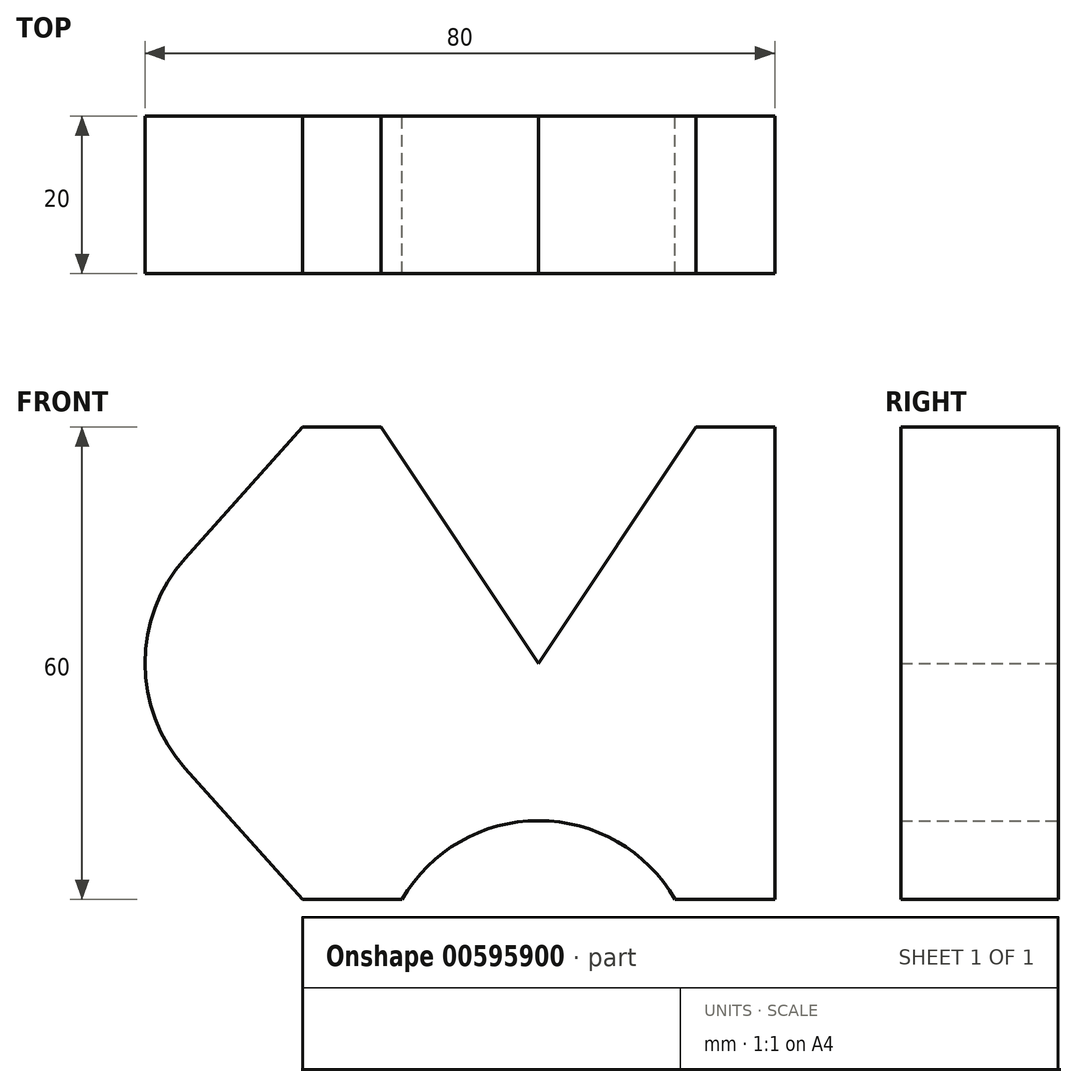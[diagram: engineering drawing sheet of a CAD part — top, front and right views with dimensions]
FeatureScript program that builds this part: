
annotation { "Feature Type Name" : "Feature", "Feature Type Description" : "" }
export const myFeature = defineFeature(function(context is Context, id is Id, definition is map)
    precondition{}
    {
        {
            var Q0;
            Q0=qCreatedBy(makeId("Front.planeOp"),FACE);
            var sketch = newSketch(context, id + "F0", { "sketchPlane" : qUnion([Q0])});
            skLineSegment(sketch, "E0", {"start": v(0, 0) * mm, "end": v(20, 30) * mm});
            skLineSegment(sketch, "E1", {"start": v(20, 30) * mm, "end": v(30, 30) * mm});
            skLineSegment(sketch, "E2", {"start": v(30, 30) * mm, "end": v(30, -30) * mm});
            skLineSegment(sketch, "E3", {"start": v(30, -30) * mm, "end": v(17.32, -30) * mm});
            skArc(sketch, "E4", {"start": v(17.32, -30) * mm, "mid": v(0, -20) * mm, "end": v(-17.32, -30) * mm});
            skLineSegment(sketch, "E5", {"start": v(-17.32, -30) * mm, "end": v(-30, -30) * mm});
            skLineSegment(sketch, "E6", {"start": v(-30, -30) * mm, "end": v(-44.9, -13.33) * mm});
            skArc(sketch, "E7", {"start": v(-44.9, 13.33) * mm, "mid": v(-50, 0) * mm, "end": v(-44.9, -13.33) * mm});
            skLineSegment(sketch, "E8", {"start": v(-44.9, 13.33) * mm, "end": v(-30, 30) * mm});
            skLineSegment(sketch, "E9", {"start": v(-30, 30) * mm, "end": v(-20, 30) * mm});
            skLineSegment(sketch, "E10", {"start": v(-20, 30) * mm, "end": v(0, 0) * mm});
            skLineSegment(sketch, "E11", {"start": v(-30, 30) * mm, "end": v(-30, -30) * mm, "construction": true});
            skSolve(sketch);
        }
        {
            var Q0;
            Q0=makeQuery(id+"F0.imprint","IMPRINT",FACE,{"disambiguationData":[TD([[makeQuery(id+"F0.imprint","IMPRINT",EDGE,{"derivedFrom":sQuery(id+"F0.wireOp",EDGE,"E0")}),-1.0]])]});
            extrude(context, id + "F1", {"entities" : qUnion([Q0]), "depth" : 20 * mm, "offsetDistance" : 25 * mm});
        }
    });
